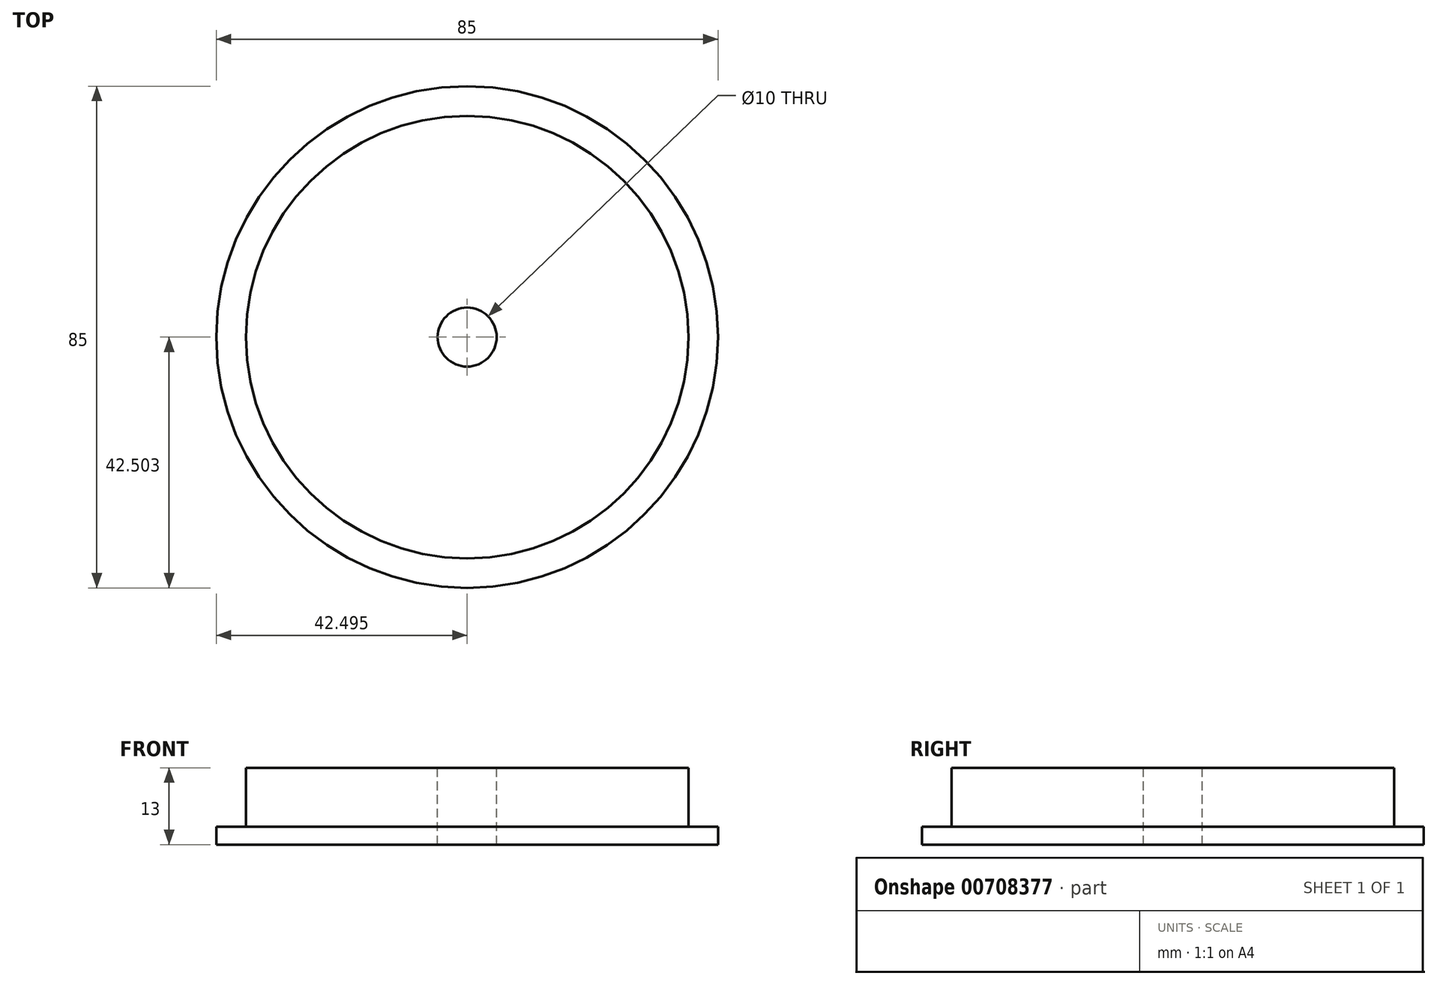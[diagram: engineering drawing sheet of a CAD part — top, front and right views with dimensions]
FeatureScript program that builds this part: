
annotation { "Feature Type Name" : "Feature", "Feature Type Description" : "" }
export const myFeature = defineFeature(function(context is Context, id is Id, definition is map)
    precondition{}
    {
        {
            var Q0;
            Q0=qCreatedBy(makeId("Top.planeOp"),FACE);
            var sketch = newSketch(context, id + "F0", { "sketchPlane" : qUnion([Q0])});
            skCircle(sketch, "E0", {"center": v(33.37, 48.67) * mm, "radius": 10 * mm});
            skCircle(sketch, "E1", {"center": v(62.3, -19.81) * mm, "radius": 15 * mm});
            skCircle(sketch, "E2", {"center": v(1.7, -19.81) * mm, "radius": 15 * mm});
            skCircle(sketch, "E3", {"center": v(-126.65, -1.92) * mm, "radius": 15 * mm});
            skCircle(sketch, "E4", {"center": v(-77.32, 5.6) * mm, "radius": 7.5 * mm});
            skCircle(sketch, "E5", {"center": v(32, 10.7) * mm, "radius": 28 * mm});
            skLineSegment(sketch, "E6", {"start": v(-126.1, -19.81) * mm, "end": v(148.49, -19.81) * mm, "construction": true});
            skLineSegment(sketch, "E7", {"start": v(1.49, 28.97) * mm, "end": v(-70.03, 0) * mm});
            skLineSegment(sketch, "E8", {"start": v(1.49, 28.97) * mm, "end": v(-99.75, 28.97) * mm});
            skLineSegment(sketch, "E9", {"start": v(-6.04, -35.66) * mm, "end": v(7.83, -39.82) * mm});
            skLineSegment(sketch, "E10", {"start": v(7.83, -39.82) * mm, "end": v(3.86, -36.45) * mm});
            skLineSegment(sketch, "E11", {"start": v(3.86, -36.45) * mm, "end": v(3.86, -42.8) * mm});
            skLineSegment(sketch, "E12", {"start": v(3.86, -42.8) * mm, "end": v(7.83, -39.82) * mm});
            skLineSegment(sketch, "E13", {"start": v(52.75, -34.5) * mm, "end": v(66.62, -38.66) * mm});
            skLineSegment(sketch, "E14", {"start": v(66.62, -38.66) * mm, "end": v(62.65, -35.29) * mm});
            skLineSegment(sketch, "E15", {"start": v(62.65, -35.29) * mm, "end": v(62.65, -41.63) * mm});
            skLineSegment(sketch, "E16", {"start": v(62.65, -41.63) * mm, "end": v(66.62, -38.66) * mm});
            skLineSegment(sketch, "E17.MirrorCS", {"start": v(24.5, 56.82) * mm, "end": v(21.5, 59.07) * mm});
            skLineSegment(sketch, "E18.MirrorCS", {"start": v(24.5, 63.16) * mm, "end": v(24.5, 56.82) * mm});
            skLineSegment(sketch, "E19.MirrorCS", {"start": v(21.5, 59.07) * mm, "end": v(24.5, 63.16) * mm});
            skLineSegment(sketch, "E20.MirrorCS", {"start": v(34.69, 63.02) * mm, "end": v(21.5, 59.07) * mm});
            skLineSegment(sketch, "E21", {"start": v(-64.9, 64.62) * mm, "end": v(-51.02, 60.46) * mm});
            skLineSegment(sketch, "E22", {"start": v(-51.02, 60.46) * mm, "end": v(-54.99, 63.83) * mm});
            skLineSegment(sketch, "E23", {"start": v(-54.99, 63.83) * mm, "end": v(-54.99, 57.49) * mm});
            skLineSegment(sketch, "E24", {"start": v(-54.99, 57.49) * mm, "end": v(-51.02, 60.46) * mm});
            skLineSegment(sketch, "E25.MirrorCS", {"start": v(-144.84, 10.33) * mm, "end": v(-147.84, 12.58) * mm});
            skLineSegment(sketch, "E26.MirrorCS", {"start": v(-144.84, 16.67) * mm, "end": v(-144.84, 10.33) * mm});
            skLineSegment(sketch, "E27.MirrorCS", {"start": v(-147.84, 12.58) * mm, "end": v(-144.84, 16.67) * mm});
            skLineSegment(sketch, "E28.MirrorCS", {"start": v(-134.66, 16.53) * mm, "end": v(-147.84, 12.58) * mm});
            skLineSegment(sketch, "E29", {"start": v(-79.9, 19.45) * mm, "end": v(-66.03, 15.3) * mm});
            skLineSegment(sketch, "E30", {"start": v(-66.03, 15.3) * mm, "end": v(-70, 18.66) * mm});
            skLineSegment(sketch, "E31", {"start": v(-70, 18.66) * mm, "end": v(-70, 12.32) * mm});
            skLineSegment(sketch, "E32", {"start": v(-70, 12.32) * mm, "end": v(-66.03, 15.3) * mm});
            skCircle(sketch, "E33", {"center": v(-113.58, -86.85) * mm, "radius": 37.5 * mm});
            skCircle(sketch, "E34", {"center": v(-113.58, -86.85) * mm, "radius": 42.5 * mm});
            skCircle(sketch, "E35", {"center": v(-113.58, -86.85) * mm, "radius": 5 * mm});
            skSolve(sketch);
        }
        {
            var Q0;
            Q0=makeQuery(id+"F0.imprint","IMPRINT",FACE,{"disambiguationData":[TD([[makeQuery(id+"F0.imprint","IMPRINT",EDGE,{"derivedFrom":sQuery(id+"F0.wireOp",EDGE,"E33")}),-1.0]])]});
            var Q1;
            Q1=makeQuery(id+"F0.imprint","IMPRINT",FACE,{"disambiguationData":[TD([[makeQuery(id+"F0.imprint","IMPRINT",EDGE,{"derivedFrom":sQuery(id+"F0.wireOp",EDGE,"E33")}),1.0]])]});
            extrude(context, id + "F1", {"entities" : qUnion([Q0, Q1]), "oppositeDirection" : true, "depth" : 3 * mm, "offsetDistance" : 25 * mm});
        }
        {
            var Q0;
            Q0=makeQuery(id+"F0.imprint","IMPRINT",FACE,{"disambiguationData":[TD([[makeQuery(id+"F0.imprint","IMPRINT",EDGE,{"derivedFrom":sQuery(id+"F0.wireOp",EDGE,"E33")}),1.0]])]});
            extrude(context, id + "F2", {"entities" : qUnion([Q0]), "operationType" : NewBodyOperationType.ADD, "depth" : 10 * mm, "offsetDistance" : 25 * mm});
        }
    });
